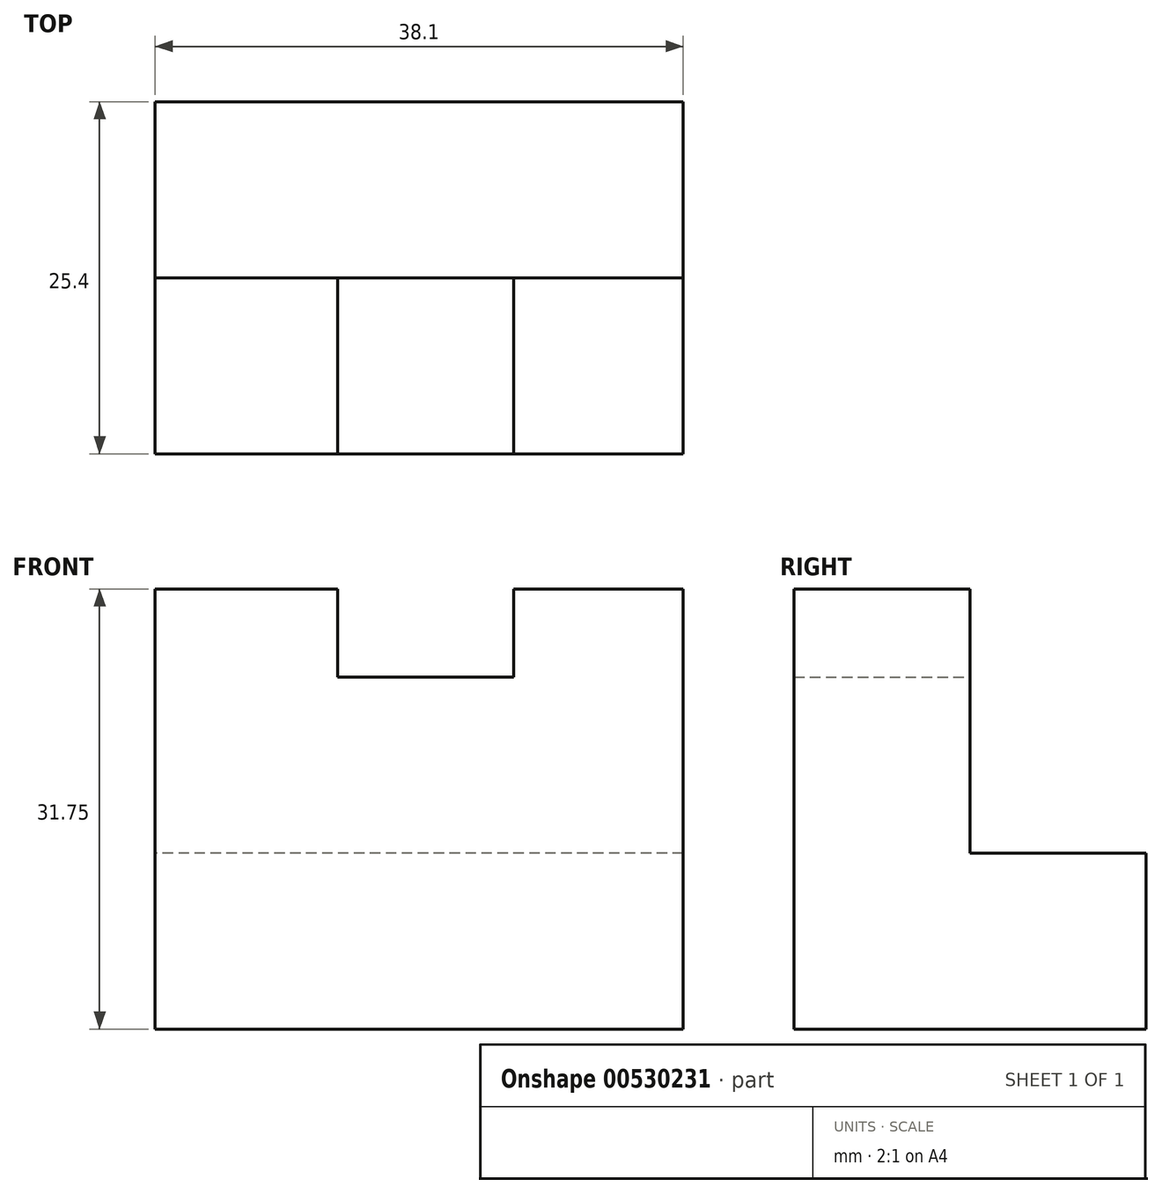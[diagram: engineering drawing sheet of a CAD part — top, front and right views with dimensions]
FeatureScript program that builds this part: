
annotation { "Feature Type Name" : "Feature", "Feature Type Description" : "" }
export const myFeature = defineFeature(function(context is Context, id is Id, definition is map)
    precondition{}
    {
        {
            var Q0;
            Q0=qCreatedBy(makeId("Front.planeOp"),FACE);
            var sketch = newSketch(context, id + "F0", { "sketchPlane" : qUnion([Q0])});
            skLineSegment(sketch, "E0", {"start": v(-60.75, 0) * mm, "end": v(-22.65, 0) * mm});
            skLineSegment(sketch, "E1", {"start": v(-22.65, 0) * mm, "end": v(-22.65, 31.75) * mm});
            skLineSegment(sketch, "E2", {"start": v(-22.65, 31.75) * mm, "end": v(-60.75, 31.75) * mm});
            skLineSegment(sketch, "E3", {"start": v(-60.75, 31.75) * mm, "end": v(-60.75, 0) * mm});
            skSolve(sketch);
        }
        {
            var Q0;
            Q0=makeQuery(id+"F0.imprint","IMPRINT",FACE,{"disambiguationData":[TD([[makeQuery(id+"F0.imprint","IMPRINT",EDGE,{"derivedFrom":sQuery(id+"F0.wireOp",EDGE,"E0")}),1.0]])]});
            extrude(context, id + "F1", {"entities" : qUnion([Q0]), "depth" : 25.4 * mm, "offsetDistance" : 25.4 * mm});
        }
        {
            var Q0;
            Q0=makeQuery(id+"F1.opExtrude","SWEPT_FACE",FACE,{"disambiguationData":[OSD([sQuery(id+"F0.wireOp",EDGE,"E3")])]});
            var sketch = newSketch(context, id + "F2", { "sketchPlane" : qUnion([Q0])});
            skLineSegment(sketch, "E4", {"start": v(12.7, 31.75) * mm, "end": v(12.7, 12.7) * mm});
            skPoint(sketch, "E4.endSnap0", {"position": v(12.7, 31.75) * mm});
            skLineSegment(sketch, "E5", {"start": v(12.7, 12.7) * mm, "end": v(0, 12.7) * mm});
            skSolve(sketch);
        }
        {
            var Q0;
            {var subQ0=sQuery(id+"F2.wireOp",EDGE,"E4");Q0=makeQuery(id+"F2.imprint","IMPRINT",FACE,{"disambiguationData":[TD([[makeQuery(id+"F2.imprint","IMPRINT",EDGE,{"derivedFrom":subQ0}),-1.0]])]});}
            extrude(context, id + "F3", {"entities" : qUnion([Q0]), "operationType" : NewBodyOperationType.REMOVE, "oppositeDirection" : true, "depth" : 254 * mm, "offsetDistance" : 25.4 * mm});
        }
        {
            var Q0;
            Q0=makeQuery(id+"F3.boolean.opBoolean","COPY",FACE,{"derivedFrom":makeQuery(id+"F3.opExtrude","SWEPT_FACE",FACE,{"disambiguationData":[OSD([sQuery(id+"F2.wireOp",EDGE,"E4")])]})});
            var sketch = newSketch(context, id + "F4", { "sketchPlane" : qUnion([Q0])});
            skLineSegment(sketch, "E6", {"start": v(34.88, 31.75) * mm, "end": v(34.88, 25.4) * mm});
            skLineSegment(sketch, "E7", {"start": v(34.88, 25.4) * mm, "end": v(47.58, 25.4) * mm});
            skLineSegment(sketch, "E8", {"start": v(47.58, 25.4) * mm, "end": v(47.58, 31.75) * mm});
            skLineSegment(sketch, "E9", {"start": v(47.58, 31.75) * mm, "end": v(34.88, 31.75) * mm});
            skSolve(sketch);
        }
        {
            var Q0;
            Q0=makeQuery(id+"F4.imprint","IMPRINT",FACE,{"disambiguationData":[TD([[makeQuery(id+"F4.imprint","IMPRINT",EDGE,{"derivedFrom":sQuery(id+"F4.wireOp",EDGE,"E6")}),1.0]])]});
            extrude(context, id + "F5", {"entities" : qUnion([Q0]), "operationType" : NewBodyOperationType.REMOVE, "oppositeDirection" : true, "depth" : 25.4 * mm, "offsetDistance" : 25.4 * mm});
        }
    });
